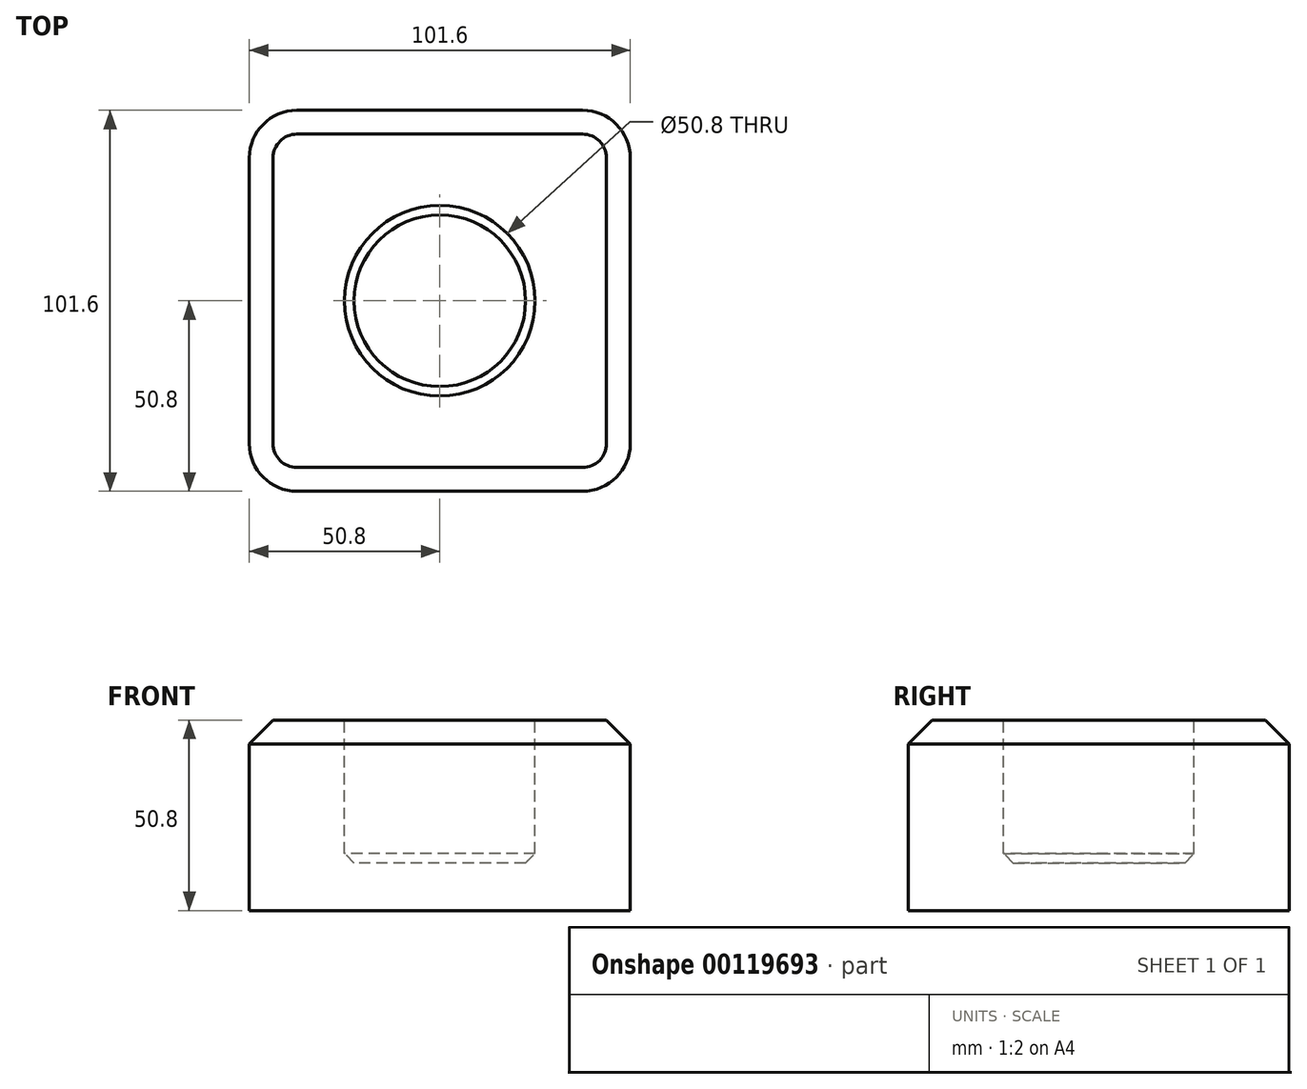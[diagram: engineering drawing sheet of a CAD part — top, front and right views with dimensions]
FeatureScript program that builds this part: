
annotation { "Feature Type Name" : "Feature", "Feature Type Description" : "" }
export const myFeature = defineFeature(function(context is Context, id is Id, definition is map)
    precondition{}
    {
        {
            var Q0;
            Q0=qCreatedBy(makeId("Top.planeOp"),FACE);
            var sketch = newSketch(context, id + "F0", { "sketchPlane" : qUnion([Q0])});
            skLineSegment(sketch, "E0.bottom", {"start": v(0, 0) * mm, "end": v(101.6, 0) * mm});
            skLineSegment(sketch, "E0.top", {"start": v(0, 101.6) * mm, "end": v(101.6, 101.6) * mm});
            skLineSegment(sketch, "E0.left", {"start": v(0, 0) * mm, "end": v(0, 101.6) * mm});
            skLineSegment(sketch, "E0.right", {"start": v(101.6, 0) * mm, "end": v(101.6, 101.6) * mm});
            skSolve(sketch);
        }
        {
            var Q0;
            Q0=makeQuery(id+"F0.imprint","IMPRINT",FACE,{"disambiguationData":[TD([[makeQuery(id+"F0.imprint","IMPRINT",EDGE,{"derivedFrom":sQuery(id+"F0.wireOp",EDGE,"E0.bottom")}),1.0]])]});
            extrude(context, id + "F1", {"entities" : qUnion([Q0]), "depth" : 50.8 * mm});
        }
        {
            var Q0;
            Q0=makeQuery(id+"F1.opExtrude","CAP_FACE",FACE,{"disambiguationData":[OSD([sQuery(id+"F0.wireOp",EDGE,"E0.bottom"),sQuery(id+"F0.wireOp",EDGE,"E0.top"),sQuery(id+"F0.wireOp",EDGE,"E0.left"),sQuery(id+"F0.wireOp",EDGE,"E0.right")])],"isStart":false});
            var sketch = newSketch(context, id + "F2", { "sketchPlane" : qUnion([Q0])});
            skCircle(sketch, "E1", {"center": v(50.8, 50.8) * mm, "radius": 25.4 * mm});
            skPoint(sketch, "E2", {"position": v(0, 50.8) * mm});
            skPoint(sketch, "E3", {"position": v(50.8, 0) * mm});
            skSolve(sketch);
        }
        {
            var Q0;
            Q0=makeQuery(id+"F2.imprint","IMPRINT",FACE,{"disambiguationData":[TD([[makeQuery(id+"F2.imprint","IMPRINT",EDGE,{"derivedFrom":sQuery(id+"F2.wireOp",EDGE,"E1")}),1.0]])]});
            extrude(context, id + "F3", {"entities" : qUnion([Q0]), "operationType" : NewBodyOperationType.REMOVE, "oppositeDirection" : true, "depth" : 38.1 * mm});
        }
        {
            var Q0;
            Q0=makeQuery(id+"F1.opExtrude","SWEPT_EDGE",EDGE,{"disambiguationData":[OSD([sQuery(id+"F0.wireOp",EDGE,"E0.bottom"),sQuery(id+"F0.wireOp",EDGE,"E0.right")])]});
            var Q1;
            Q1=makeQuery(id+"F1.opExtrude","SWEPT_EDGE",EDGE,{"disambiguationData":[OSD([sQuery(id+"F0.wireOp",EDGE,"E0.bottom"),sQuery(id+"F0.wireOp",EDGE,"E0.left")])]});
            var Q2;
            Q2=makeQuery(id+"F1.opExtrude","SWEPT_EDGE",EDGE,{"disambiguationData":[OSD([sQuery(id+"F0.wireOp",EDGE,"E0.top"),sQuery(id+"F0.wireOp",EDGE,"E0.right")])]});
            var Q3;
            Q3=makeQuery(id+"F1.opExtrude","SWEPT_EDGE",EDGE,{"disambiguationData":[OSD([sQuery(id+"F0.wireOp",EDGE,"E0.top"),sQuery(id+"F0.wireOp",EDGE,"E0.left")])]});
            fillet(context, id + "F4", {"entities" : qUnion([Q0, Q1, Q2, Q3]), "radius" : 12.7 * mm, "tangentPropagation" : true, "allowEdgeOverflow" : false});
        }
        {
            var Q0;
            Q0=makeQuery(id+"F3.boolean.opBoolean","COPY",EDGE,{"derivedFrom":makeQuery(id+"F3.opExtrude","CAP_EDGE",EDGE,{"disambiguationData":[OSD([sQuery(id+"F2.wireOp",EDGE,"E1")])],"isStart":false})});
            var Q1;
            Q1=makeQuery(id+"F3.boolean.opBoolean","COPY",EDGE,{"derivedFrom":makeQuery(id+"F3.opExtrude","CAP_EDGE",EDGE,{"disambiguationData":[OSD([sQuery(id+"F2.wireOp",EDGE,"E1")])],"isStart":true})});
            chamfer(context, id + "F5", {"entities" : qUnion([Q0, Q1]), "width" : 2.54 * mm, "tangentPropagation" : true});
        }
        {
            var Q0;
            Q0=makeQuery(id+"F1.opExtrude","CAP_EDGE",EDGE,{"disambiguationData":[OSD([sQuery(id+"F0.wireOp",EDGE,"E0.left")])],"isStart":false});
            chamfer(context, id + "F6", {"entities" : qUnion([Q0]), "width" : 6.35 * mm, "tangentPropagation" : true});
        }
    });
